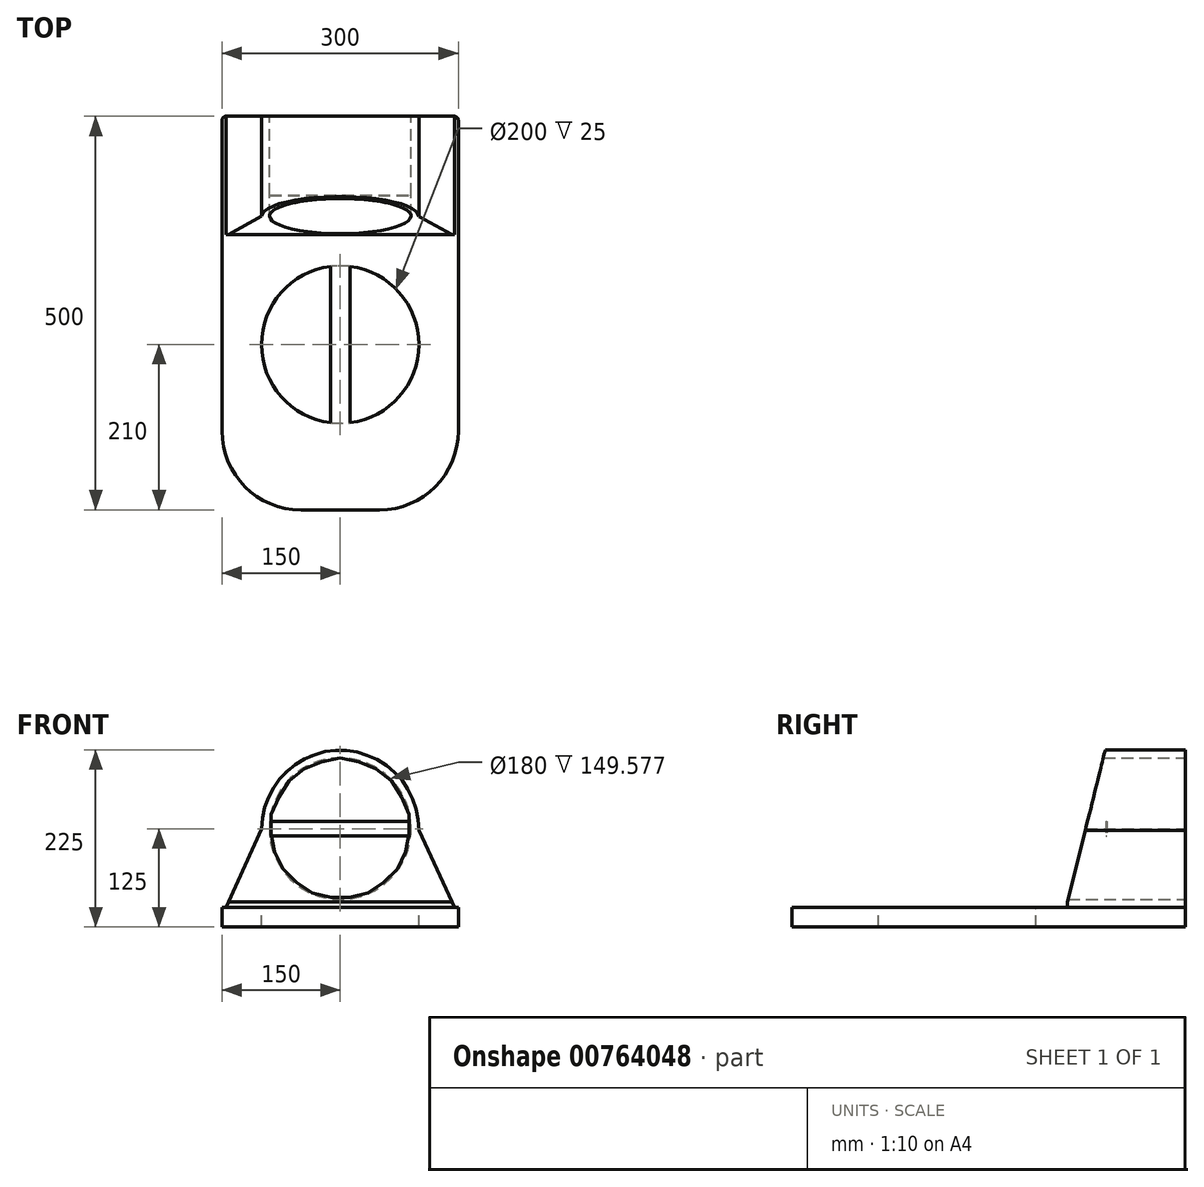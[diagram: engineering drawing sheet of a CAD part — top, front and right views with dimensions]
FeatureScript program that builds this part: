
annotation { "Feature Type Name" : "Feature", "Feature Type Description" : "" }
export const myFeature = defineFeature(function(context is Context, id is Id, definition is map)
    precondition{}
    {
        {
            var Q0;
            Q0=qCreatedBy(makeId("Top.planeOp"),FACE);
            var sketch = newSketch(context, id + "F0", { "sketchPlane" : qUnion([Q0])});
            skLineSegment(sketch, "E0.bottom", {"start": v(-50, -250) * mm, "end": v(50, -250) * mm});
            skLineSegment(sketch, "E0.top", {"start": v(-150, 250) * mm, "end": v(150, 250) * mm});
            skLineSegment(sketch, "E0.left", {"start": v(-150, -150) * mm, "end": v(-150, 250) * mm});
            skLineSegment(sketch, "E0.right", {"start": v(150, -150) * mm, "end": v(150, 250) * mm});
            skPoint(sketch, "E0.middle", {"position": v(0, 0) * mm});
            skPoint(sketch, "E1.visualSharp", {"position": v(-150, -250) * mm});
            skArc(sketch, "E1.filletArc", {"start": v(-150, -150) * mm, "mid": v(-120.71, -220.71) * mm, "end": v(-50, -250) * mm});
            skPoint(sketch, "E2.visualSharp", {"position": v(150, -250) * mm});
            skArc(sketch, "E2.filletArc", {"start": v(50, -250) * mm, "mid": v(120.71, -220.71) * mm, "end": v(150, -150) * mm});
            skPoint(sketch, "E3", {"position": v(0, -40) * mm});
            skCircle(sketch, "E4", {"center": v(0, -40) * mm, "radius": 100 * mm});
            skSolve(sketch);
        }
        {
            var Q0;
            Q0 = qSketchRegion(id + "F0", true);
            extrude(context, id + "F1", {"entities" : qUnion([Q0]), "oppositeDirection" : true, "depth" : 25 * mm, "offsetDistance" : 25 * mm});
        }
        {
            var Q0;
            Q0=makeQuery(id+"F1.opExtrude","SWEPT_EDGE",EDGE,{"disambiguationData":[OSD([sQuery(id+"F0.wireOp",EDGE,"E0.top"),sQuery(id+"F0.wireOp",EDGE,"E0.right")])]});
            var Q1;
            Q1=makeQuery(id+"F1.opExtrude","SWEPT_EDGE",EDGE,{"disambiguationData":[OSD([sQuery(id+"F0.wireOp",EDGE,"E0.top"),sQuery(id+"F0.wireOp",EDGE,"E0.left")])]});
            fillet(context, id + "F2", {"entities" : qUnion([Q0, Q1]), "radius" : 5 * mm, "tangentPropagation" : true, "allowEdgeOverflow" : false});
        }
        {
            var Q0;
            Q0=makeQuery(id+"F1.opExtrude","SWEPT_FACE",FACE,{"disambiguationData":[OSD([sQuery(id+"F0.wireOp",EDGE,"E0.top")])]});
            var sketch = newSketch(context, id + "F3", { "sketchPlane" : qUnion([Q0])});
            skPoint(sketch, "E5", {"position": v(0, 100) * mm});
            skPoint(sketch, "E5.positionSnap0", {"position": v(0, 0) * mm});
            skCircle(sketch, "E6", {"center": v(0, 100) * mm, "radius": 100 * mm});
            skLineSegment(sketch, "E7", {"start": v(-99.98, 97.97) * mm, "end": v(-145, 0) * mm});
            skLineSegment(sketch, "E8", {"start": v(100, 100) * mm, "end": v(145, 0) * mm});
            skCircle(sketch, "E9", {"center": v(0, 100) * mm, "radius": 90 * mm});
            skSolve(sketch);
        }
        {
            var Q0;
            Q0 = qSketchRegion(id + "F3", true);
            var Q1;
            {var subQ0=sQuery(id+"F3.wireOp",EDGE,"E7");Q1=makeQuery(id+"F3.imprint","IMPRINT",FACE,{"disambiguationData":[TD([[makeQuery(id+"F3.imprint","IMPRINT",EDGE,{"derivedFrom":subQ0}),1.0]])]});}
            var Q2;
            {var subQ0=sQuery(id+"F3.wireOp",EDGE,"E8");Q2=makeQuery(id+"F3.imprint","IMPRINT",FACE,{"disambiguationData":[TD([[makeQuery(id+"F3.imprint","IMPRINT",EDGE,{"derivedFrom":subQ0}),-1.0]])]});}
            extrude(context, id + "F4", {"entities" : qUnion([Q0, Q1, Q2]), "operationType" : NewBodyOperationType.ADD, "oppositeDirection" : true, "depth" : 150 * mm, "offsetDistance" : 25 * mm});
        }
        {
            var Q0;
            Q0=makeQuery(id+"F1.opExtrude","SWEPT_FACE",FACE,{"disambiguationData":[OSD([sQuery(id+"F0.wireOp",EDGE,"E0.right")])]});
            var sketch = newSketch(context, id + "F5", { "sketchPlane" : qUnion([Q0])});
            skLineSegment(sketch, "E10.right", {"start": v(98.24, 0) * mm, "end": v(98.24, 200.66) * mm});
            skLineSegment(sketch, "E11", {"start": v(98.24, 200.66) * mm, "end": v(148.24, 200.66) * mm});
            skLineSegment(sketch, "E12", {"start": v(148.24, 200.66) * mm, "end": v(98.24, 0) * mm});
            skSolve(sketch);
        }
        {
            var Q0;
            Q0 = qSketchRegion(id + "F5", true);
            extrude(context, id + "F6", {"entities" : qUnion([Q0]), "operationType" : NewBodyOperationType.REMOVE, "endBound" : BoundingType.THROUGH_ALL, "oppositeDirection" : true, "depth" : 25 * mm, "offsetDistance" : 25 * mm});
        }
        {
            var Q0;
            Q0=makeQuery(id+"F1.opExtrude","CAP_FACE",FACE,{"disambiguationData":[OSD([sQuery(id+"F0.wireOp",EDGE,"E0.bottom"),sQuery(id+"F0.wireOp",EDGE,"E0.top"),sQuery(id+"F0.wireOp",EDGE,"E0.left"),sQuery(id+"F0.wireOp",EDGE,"E0.right"),sQuery(id+"F0.wireOp",EDGE,"E1.filletArc"),sQuery(id+"F0.wireOp",EDGE,"E2.filletArc"),sQuery(id+"F0.wireOp",EDGE,"E4")])],"isStart":true});
            var sketch = newSketch(context, id + "F7", { "sketchPlane" : qUnion([Q0])});
            skLineSegment(sketch, "E13.bottom", {"start": v(-12.5, 60) * mm, "end": v(12.5, 60) * mm});
            skLineSegment(sketch, "E13.top", {"start": v(-12.5, -140) * mm, "end": v(12.5, -140) * mm});
            skLineSegment(sketch, "E13.left", {"start": v(-12.5, 60) * mm, "end": v(-12.5, -140) * mm});
            skLineSegment(sketch, "E13.right", {"start": v(12.5, 60) * mm, "end": v(12.5, -140) * mm});
            skPoint(sketch, "E13.middle", {"position": v(0, -40) * mm});
            skSolve(sketch);
        }
        {
            var Q0;
            Q0 = qSketchRegion(id + "F7", true);
            extrude(context, id + "F8", {"entities" : qUnion([Q0]), "operationType" : NewBodyOperationType.ADD, "oppositeDirection" : true, "depth" : 1 * mm, "offsetDistance" : 25 * mm});
        }
        {
            var Q0;
            Q0=qCreatedBy(makeId("Front.planeOp"),FACE);
            cPlane(context, id + "F9", {"entities" : qUnion([Q0]), "cplaneType" : CPlaneType.OFFSET, "offset" : 150 * mm, "oppositeDirection" : true, "width" : 150 * mm, "height" : 150 * mm});
        }
        {
            var Q0;
            Q0=qCreatedBy(id+"F9.planeOp",FACE);
            var sketch = newSketch(context, id + "F10", { "sketchPlane" : qUnion([Q0])});
            skLineSegment(sketch, "E14.bottom", {"start": v(-90, 90.58) * mm, "end": v(90, 90.58) * mm});
            skLineSegment(sketch, "E14.top", {"start": v(-90, 109.42) * mm, "end": v(90, 109.42) * mm});
            skLineSegment(sketch, "E14.left", {"start": v(-90, 90.58) * mm, "end": v(-90, 109.42) * mm});
            skLineSegment(sketch, "E14.right", {"start": v(90, 90.58) * mm, "end": v(90, 109.42) * mm});
            skPoint(sketch, "E14.middle", {"position": v(0, 100) * mm});
            skSolve(sketch);
        }
        {
            var Q0;
            Q0 = qSketchRegion(id + "F10", true);
            extrude(context, id + "F11", {"entities" : qUnion([Q0]), "operationType" : NewBodyOperationType.ADD, "depth" : 1 * mm, "offsetDistance" : 25 * mm});
        }
    });
